# Revit family: 3081025
name_source: partatom
category: Lighting Fixtures
revit_build: Autodesk Revit 2018 (Build: 20170223_1515(x64)
units: mm (PartAtom-declared; Revit-internal decimal feet)

## family parameters
Cut with Voids When Loaded = No
Host = Face
Light Source = Yes
Part Type = Normal
Room Calculation Point = No
Round Connector Dimension = Use Diameter
Shared = No

## types (1)
- 3081025 INVERTO DIRECT NW EB BLACK
    Apparent Load = 16 VA
    Assembly Code = D5020200
    AssetType = Fixed
    Calculate Coefficient of Utilization = No
    Color Filter = 16777215
    Cost = 0 $
    Default Elevation = 1219 mm
    Description = Surface Wall mounted luminaire, wire to base with pluggable connection for easy installation,  suitable for looping, black coloured aluminium housing, 1,617lm, 16W, 101lm/W, 4000K, 350mA , CRI:80,  40° beam Angle, non-dimmable, IP65, IK07, 50,000hrs (L70),  162 x 110 x 110 mm.
    Dimming Lamp Color Temperature Shift = <None>
    DocumentationLiterature = http://www.sylvania-lighting.com
    DurationUnit = hours
    ElectricShockClassification = 101
    Emit Shape Visible in Rendering = No
    Emit from Rectangle Length = 90 mm  [stored 0.295276 ft]
    Emit from Rectangle Width = 90 mm  [stored 0.295276 ft]
    ExpectedLife = 50000
    Housing material = Bronze, Architectural
    IfcExportAs = Class I
    IfcExportType = IfcLightFixtureType
    ImpactProtectionIndex = IfcLightFixtureType
    IngressProtection = IfcLightFixtureType
    InputNominalFrequency = 4000
    InputVoltage = 0
    LampColourRenderingIndex = 16500
    LampColourTemperature = LED
    LampMacAdamStep = 80
    LampNominalLuminous = 4000 K
    LightOutputRatio = LED
    LuminaireType = 0
    ManufacturerName = 101 lm/W
    Material = Feilo Sylvania
    Model = INVERTO DIRECT NW EB BLACK
    ModelNumber = 3081025
    ModelReference = INVERTO DIRECT NW EB BLACK
    Name = INVERTO DIRECT NW EB BLACK
    NominalDepth = 110 mm  [stored 0.360892 ft]
    NominalHeight = 110 mm  [stored 0.360892 ft]
    NominalLength = 110 mm  [stored 0.360892 ft]
    Photometric Web File = 3081025.ies
    PowerConsumption = Lighting
    PowerFactor = 0
    Tilt Angle = -90.00°
    Type Image = <None>
    TypeName = INVERTO DIRECT NW EB BLACK
    URL = 0.95
    Voltage = 230 V
    WarrantyDescription = http://www.sylvania-lighting.com

note: [stored X ft] marks values corroborated as IEEE doubles in the binary element streams (Revit-internal decimal feet)

## geometry (parser evidence)
native form markers: Sweep x3
no freeform markers — native parametric forms only
